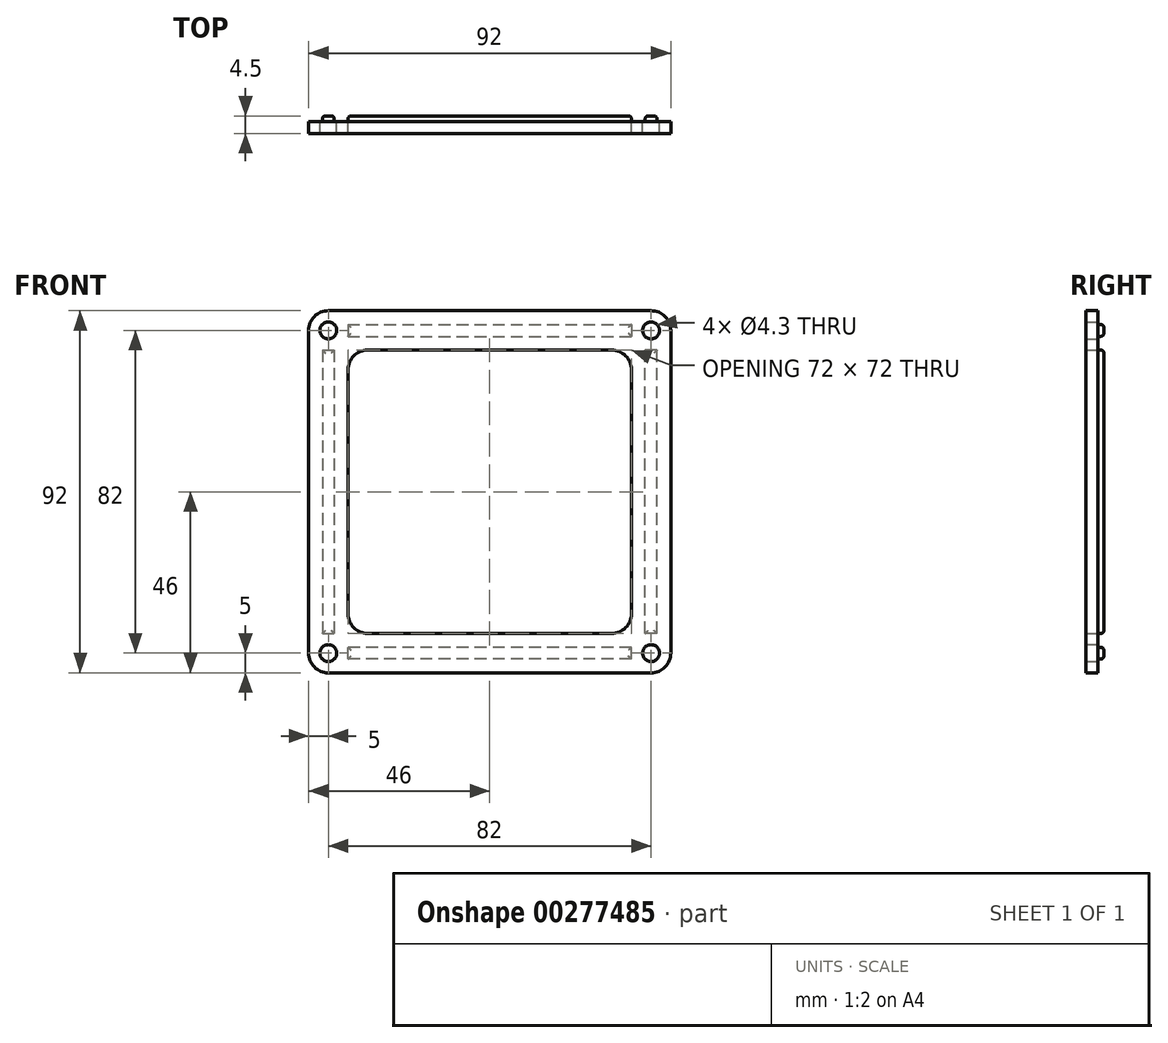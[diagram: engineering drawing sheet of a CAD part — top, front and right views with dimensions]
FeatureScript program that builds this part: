
annotation { "Feature Type Name" : "Feature", "Feature Type Description" : "" }
export const myFeature = defineFeature(function(context is Context, id is Id, definition is map)
    precondition{}
    {
        {
            var Q0;
            Q0=qCreatedBy(makeId("Front.planeOp"),FACE);
            var sketch = newSketch(context, id + "F0", { "sketchPlane" : qUnion([Q0])});
            skLineSegment(sketch, "E0.bottom", {"start": v(46, 46) * mm, "end": v(-46, 46) * mm});
            skLineSegment(sketch, "E0.top", {"start": v(46, -46) * mm, "end": v(-46, -46) * mm});
            skLineSegment(sketch, "E0.left", {"start": v(46, 46) * mm, "end": v(46, -46) * mm});
            skLineSegment(sketch, "E0.right", {"start": v(-46, 46) * mm, "end": v(-46, -46) * mm});
            skPoint(sketch, "E0.middle", {"position": v(0, 0) * mm});
            skLineSegment(sketch, "E1.0", {"start": v(-36, 36) * mm, "end": v(-36, -36) * mm});
            skLineSegment(sketch, "E1.1", {"start": v(36, 36) * mm, "end": v(-36, 36) * mm});
            skLineSegment(sketch, "E1.2", {"start": v(36, 36) * mm, "end": v(36, -36) * mm});
            skLineSegment(sketch, "E1.3", {"start": v(36, -36) * mm, "end": v(-36, -36) * mm});
            skLineSegment(sketch, "E2.0", {"start": v(-41, 41) * mm, "end": v(-41, -41) * mm, "construction": true});
            skLineSegment(sketch, "E2.1", {"start": v(41, 41) * mm, "end": v(-41, 41) * mm, "construction": true});
            skLineSegment(sketch, "E2.2", {"start": v(41, 41) * mm, "end": v(41, -41) * mm, "construction": true});
            skLineSegment(sketch, "E2.3", {"start": v(41, -41) * mm, "end": v(-41, -41) * mm, "construction": true});
            skCircle(sketch, "E3", {"center": v(-41, 41) * mm, "radius": 2.15 * mm});
            skCircle(sketch, "E4.MirrorC", {"center": v(41, 41) * mm, "radius": 2.15 * mm});
            skCircle(sketch, "E5.MirrorC", {"center": v(41, -41) * mm, "radius": 2.15 * mm});
            skCircle(sketch, "E6.MirrorC", {"center": v(-41, -41) * mm, "radius": 2.15 * mm});
            skSolve(sketch);
        }
        {
            var Q0;
            Q0 = qSketchRegion(id + "F0", true);
            extrude(context, id + "F1", {"entities" : qUnion([Q0]), "endBound" : BoundingType.SYMMETRIC, "depth" : 3 * mm});
        }
        {
            var Q0;
            Q0=makeQuery(id+"F1.opExtrude","CAP_FACE",FACE,{"disambiguationData":[OSD([sQuery(id+"F0.wireOp",EDGE,"E0.bottom"),sQuery(id+"F0.wireOp",EDGE,"E0.top"),sQuery(id+"F0.wireOp",EDGE,"E0.left"),sQuery(id+"F0.wireOp",EDGE,"E0.right"),sQuery(id+"F0.wireOp",EDGE,"E1.0"),sQuery(id+"F0.wireOp",EDGE,"E1.1"),sQuery(id+"F0.wireOp",EDGE,"E1.2"),sQuery(id+"F0.wireOp",EDGE,"E1.3"),sQuery(id+"F0.wireOp",EDGE,"E3"),sQuery(id+"F0.wireOp",EDGE,"E4.MirrorC"),sQuery(id+"F0.wireOp",EDGE,"E5.MirrorC"),sQuery(id+"F0.wireOp",EDGE,"E6.MirrorC")])],"isStart":true});
            var sketch = newSketch(context, id + "F2", { "sketchPlane" : qUnion([Q0])});
            skLineSegment(sketch, "E7.0", {"start": v(-46, 46) * mm, "end": v(46, 46) * mm, "construction": true});
            skLineSegment(sketch, "E8.0", {"start": v(-46, 46) * mm, "end": v(-46, -46) * mm, "construction": true});
            skLineSegment(sketch, "E9.0", {"start": v(-36, 36) * mm, "end": v(-36, -36) * mm, "construction": true});
            skLineSegment(sketch, "E10.0", {"start": v(-36, 36) * mm, "end": v(36, 36) * mm, "construction": true});
            skLineSegment(sketch, "E11.0", {"start": v(36, 36) * mm, "end": v(36, -36) * mm, "construction": true});
            skLineSegment(sketch, "E12.0", {"start": v(46, 46) * mm, "end": v(46, -46) * mm, "construction": true});
            skLineSegment(sketch, "E13.0", {"start": v(-46, -46) * mm, "end": v(46, -46) * mm, "construction": true});
            skLineSegment(sketch, "E14.0", {"start": v(-36, -36) * mm, "end": v(36, -36) * mm, "construction": true});
            skLineSegment(sketch, "E15", {"start": v(-41, 41) * mm, "end": v(41, 41) * mm, "construction": true});
            skLineSegment(sketch, "E16.bottom", {"start": v(36, 42.5) * mm, "end": v(-36, 42.5) * mm});
            skLineSegment(sketch, "E16.top", {"start": v(36, 39.5) * mm, "end": v(-36, 39.5) * mm});
            skLineSegment(sketch, "E16.left", {"start": v(36, 42.5) * mm, "end": v(36, 39.5) * mm});
            skLineSegment(sketch, "E16.right", {"start": v(-36, 42.5) * mm, "end": v(-36, 39.5) * mm});
            skPoint(sketch, "E16.middle", {"position": v(0, 41) * mm});
            skLineSegment(sketch, "E17", {"start": v(-46, 46) * mm, "end": v(46, -46) * mm, "construction": true});
            skLineSegment(sketch, "E18", {"start": v(-46, -46) * mm, "end": v(46, 46) * mm, "construction": true});
            skLineSegment(sketch, "E19.MirrorCS", {"start": v(-42.5, -36) * mm, "end": v(-42.5, 36) * mm});
            skLineSegment(sketch, "E20.MirrorCS", {"start": v(-39.5, -36) * mm, "end": v(-39.5, 36) * mm});
            skLineSegment(sketch, "E21.MirrorCS", {"start": v(-42.5, 36) * mm, "end": v(-39.5, 36) * mm});
            skLineSegment(sketch, "E22.MirrorCS", {"start": v(-42.5, -36) * mm, "end": v(-39.5, -36) * mm});
            skLineSegment(sketch, "E23.MirrorCS", {"start": v(42.5, 36) * mm, "end": v(42.5, -36) * mm});
            skLineSegment(sketch, "E24.MirrorCS", {"start": v(39.5, 36) * mm, "end": v(39.5, -36) * mm});
            skLineSegment(sketch, "E25.MirrorCS", {"start": v(42.5, 36) * mm, "end": v(39.5, 36) * mm});
            skPoint(sketch, "E26.MirrorP", {"position": v(41, 0) * mm});
            skLineSegment(sketch, "E27.MirrorCS", {"start": v(42.5, -36) * mm, "end": v(39.5, -36) * mm});
            skLineSegment(sketch, "E28.MirrorCS", {"start": v(-36, -39.5) * mm, "end": v(36, -39.5) * mm});
            skLineSegment(sketch, "E29.MirrorCS", {"start": v(-36, -42.5) * mm, "end": v(-36, -39.5) * mm});
            skLineSegment(sketch, "E30.MirrorCS", {"start": v(-36, -42.5) * mm, "end": v(36, -42.5) * mm});
            skLineSegment(sketch, "E31.MirrorCS", {"start": v(36, -42.5) * mm, "end": v(36, -39.5) * mm});
            skSolve(sketch);
        }
        {
            var Q0;
            Q0=makeQuery(id+"F2.imprint","IMPRINT",FACE,{"disambiguationData":[TD([[makeQuery(id+"F2.imprint","IMPRINT",EDGE,{"derivedFrom":sQuery(id+"F2.wireOp",EDGE,"E16.bottom")}),1.0]])]});
            var Q1;
            Q1=makeQuery(id+"F2.imprint","IMPRINT",FACE,{"disambiguationData":[TD([[makeQuery(id+"F2.imprint","IMPRINT",EDGE,{"derivedFrom":sQuery(id+"F2.wireOp",EDGE,"E19.MirrorCS")}),-1.0]])]});
            var Q2;
            Q2=makeQuery(id+"F2.imprint","IMPRINT",FACE,{"disambiguationData":[TD([[makeQuery(id+"F2.imprint","IMPRINT",EDGE,{"derivedFrom":sQuery(id+"F2.wireOp",EDGE,"E23.MirrorCS")}),-1.0]])]});
            var Q3;
            Q3=makeQuery(id+"F2.imprint","IMPRINT",FACE,{"disambiguationData":[TD([[makeQuery(id+"F2.imprint","IMPRINT",EDGE,{"derivedFrom":sQuery(id+"F2.wireOp",EDGE,"E28.MirrorCS")}),-1.0]])]});
            extrude(context, id + "F3", {"entities" : qUnion([Q0, Q1, Q2, Q3]), "operationType" : NewBodyOperationType.ADD, "depth" : 1.5 * mm});
        }
        {
            var Q0;
            Q0=makeQuery(id+"F1.opExtrude","SWEPT_EDGE",EDGE,{"disambiguationData":[OSD([sQuery(id+"F0.wireOp",EDGE,"E0.bottom"),sQuery(id+"F0.wireOp",EDGE,"E0.right")])]});
            var Q1;
            Q1=makeQuery(id+"F1.opExtrude","SWEPT_EDGE",EDGE,{"disambiguationData":[OSD([sQuery(id+"F0.wireOp",EDGE,"E0.bottom"),sQuery(id+"F0.wireOp",EDGE,"E0.left")])]});
            var Q2;
            Q2=makeQuery(id+"F1.opExtrude","SWEPT_EDGE",EDGE,{"disambiguationData":[OSD([sQuery(id+"F0.wireOp",EDGE,"E0.top"),sQuery(id+"F0.wireOp",EDGE,"E0.left")])]});
            var Q3;
            Q3=makeQuery(id+"F1.opExtrude","SWEPT_EDGE",EDGE,{"disambiguationData":[OSD([sQuery(id+"F0.wireOp",EDGE,"E0.top"),sQuery(id+"F0.wireOp",EDGE,"E0.right")])]});
            var Q4;
            Q4=makeQuery(id+"F1.opExtrude","SWEPT_EDGE",EDGE,{"disambiguationData":[OSD([sQuery(id+"F0.wireOp",EDGE,"E1.2"),sQuery(id+"F0.wireOp",EDGE,"E1.3")])]});
            var Q5;
            Q5=makeQuery(id+"F1.opExtrude","SWEPT_EDGE",EDGE,{"disambiguationData":[OSD([sQuery(id+"F0.wireOp",EDGE,"E1.0"),sQuery(id+"F0.wireOp",EDGE,"E1.3")])]});
            var Q6;
            Q6=makeQuery(id+"F1.opExtrude","SWEPT_EDGE",EDGE,{"disambiguationData":[OSD([sQuery(id+"F0.wireOp",EDGE,"E1.1"),sQuery(id+"F0.wireOp",EDGE,"E1.2")])]});
            var Q7;
            Q7=makeQuery(id+"F1.opExtrude","SWEPT_EDGE",EDGE,{"disambiguationData":[OSD([sQuery(id+"F0.wireOp",EDGE,"E1.0"),sQuery(id+"F0.wireOp",EDGE,"E1.1")])]});
            fillet(context, id + "F4", {"entities" : qUnion([Q0, Q1, Q2, Q3, Q4, Q5, Q6, Q7]), "radius" : 5 * mm, "tangentPropagation" : true, "allowEdgeOverflow" : false});
        }
        {
            var Q0;
            Q0=makeQuery(id+"F3.opExtrude","CAP_EDGE",EDGE,{"disambiguationData":[OSD([sQuery(id+"F2.wireOp",EDGE,"E20.MirrorCS")])],"isStart":false});
            var Q1;
            Q1=makeQuery(id+"F3.opExtrude","CAP_EDGE",EDGE,{"disambiguationData":[OSD([sQuery(id+"F2.wireOp",EDGE,"E19.MirrorCS")])],"isStart":false});
            var Q2;
            Q2=makeQuery(id+"F3.opExtrude","CAP_EDGE",EDGE,{"disambiguationData":[OSD([sQuery(id+"F2.wireOp",EDGE,"E22.MirrorCS")])],"isStart":false});
            var Q3;
            Q3=makeQuery(id+"F3.opExtrude","CAP_EDGE",EDGE,{"disambiguationData":[OSD([sQuery(id+"F2.wireOp",EDGE,"E21.MirrorCS")])],"isStart":false});
            var Q4;
            Q4=makeQuery(id+"F3.opExtrude","CAP_EDGE",EDGE,{"disambiguationData":[OSD([sQuery(id+"F2.wireOp",EDGE,"E16.bottom")])],"isStart":false});
            var Q5;
            Q5=makeQuery(id+"F3.opExtrude","CAP_EDGE",EDGE,{"disambiguationData":[OSD([sQuery(id+"F2.wireOp",EDGE,"E16.right")])],"isStart":false});
            var Q6;
            Q6=makeQuery(id+"F3.opExtrude","CAP_EDGE",EDGE,{"disambiguationData":[OSD([sQuery(id+"F2.wireOp",EDGE,"E16.top")])],"isStart":false});
            var Q7;
            Q7=makeQuery(id+"F3.opExtrude","CAP_EDGE",EDGE,{"disambiguationData":[OSD([sQuery(id+"F2.wireOp",EDGE,"E16.left")])],"isStart":false});
            var Q8;
            Q8=makeQuery(id+"F3.opExtrude","CAP_EDGE",EDGE,{"disambiguationData":[OSD([sQuery(id+"F2.wireOp",EDGE,"E25.MirrorCS")])],"isStart":false});
            var Q9;
            Q9=makeQuery(id+"F3.opExtrude","CAP_EDGE",EDGE,{"disambiguationData":[OSD([sQuery(id+"F2.wireOp",EDGE,"E24.MirrorCS")])],"isStart":false});
            var Q10;
            Q10=makeQuery(id+"F3.opExtrude","CAP_EDGE",EDGE,{"disambiguationData":[OSD([sQuery(id+"F2.wireOp",EDGE,"E23.MirrorCS")])],"isStart":false});
            var Q11;
            Q11=makeQuery(id+"F3.opExtrude","CAP_EDGE",EDGE,{"disambiguationData":[OSD([sQuery(id+"F2.wireOp",EDGE,"E27.MirrorCS")])],"isStart":false});
            var Q12;
            Q12=makeQuery(id+"F3.opExtrude","CAP_EDGE",EDGE,{"disambiguationData":[OSD([sQuery(id+"F2.wireOp",EDGE,"E31.MirrorCS")])],"isStart":false});
            var Q13;
            Q13=makeQuery(id+"F3.opExtrude","CAP_EDGE",EDGE,{"disambiguationData":[OSD([sQuery(id+"F2.wireOp",EDGE,"E28.MirrorCS")])],"isStart":false});
            var Q14;
            Q14=makeQuery(id+"F3.opExtrude","CAP_EDGE",EDGE,{"disambiguationData":[OSD([sQuery(id+"F2.wireOp",EDGE,"E29.MirrorCS")])],"isStart":false});
            var Q15;
            Q15=makeQuery(id+"F3.opExtrude","CAP_EDGE",EDGE,{"disambiguationData":[OSD([sQuery(id+"F2.wireOp",EDGE,"E30.MirrorCS")])],"isStart":false});
            fillet(context, id + "F5", {"entities" : qUnion([Q0, Q1, Q2, Q3, Q4, Q5, Q6, Q7, Q8, Q9, Q10, Q11, Q12, Q13, Q14, Q15]), "radius" : .75 * mm, "tangentPropagation" : true, "allowEdgeOverflow" : false});
        }
    });
